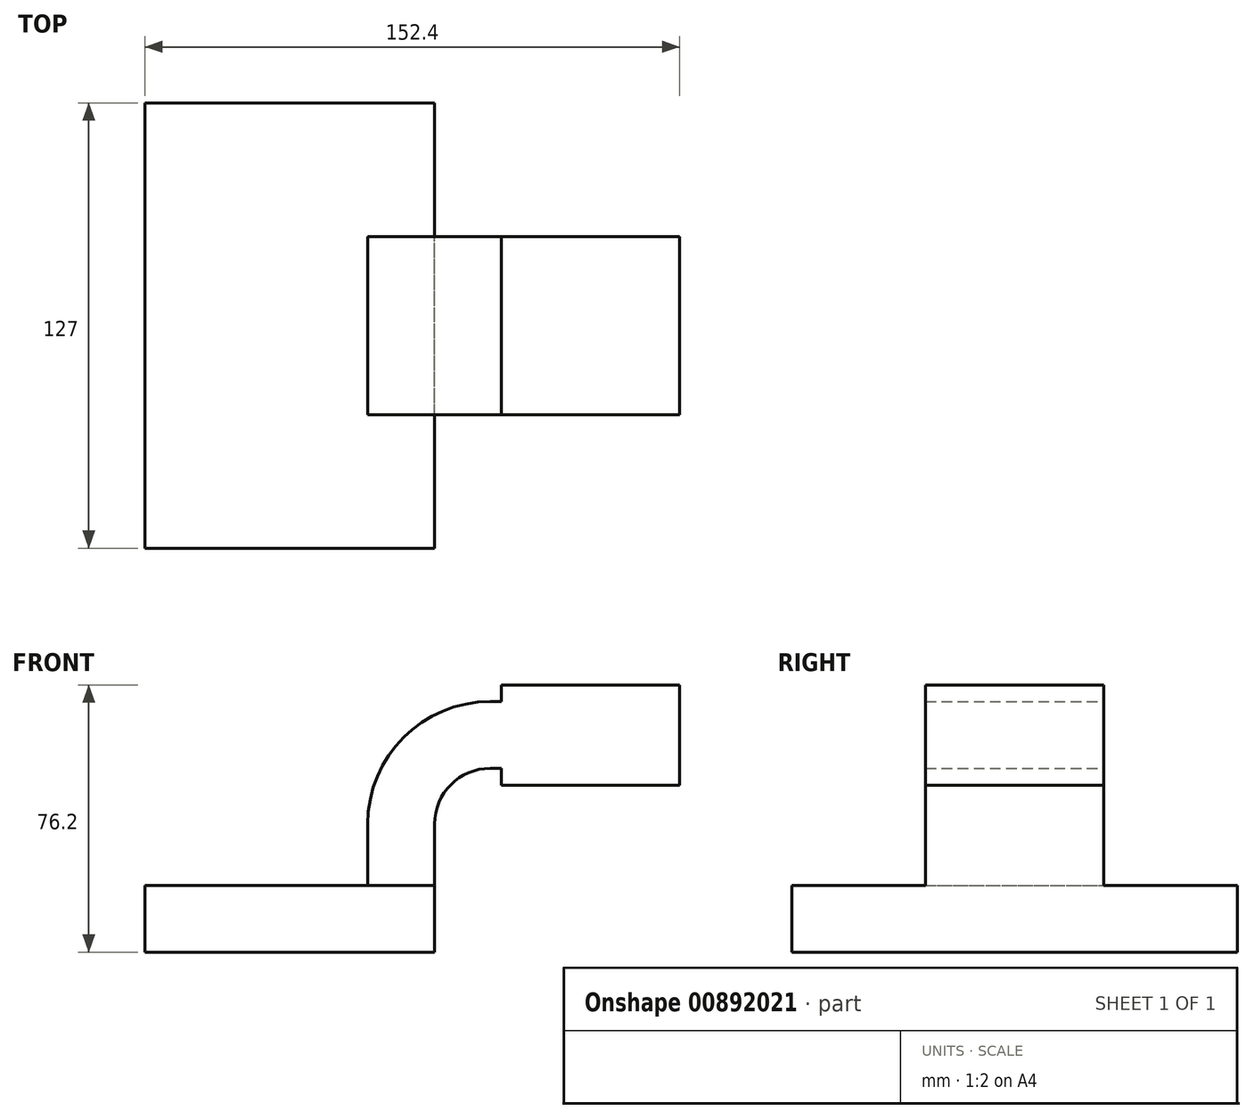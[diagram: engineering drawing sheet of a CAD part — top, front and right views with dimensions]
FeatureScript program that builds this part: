
annotation { "Feature Type Name" : "Feature", "Feature Type Description" : "" }
export const myFeature = defineFeature(function(context is Context, id is Id, definition is map)
    precondition{}
    {
        {
            var Q0;
            Q0=qCreatedBy(makeId("Front.planeOp"),FACE);
            var sketch = newSketch(context, id + "F0", { "sketchPlane" : qUnion([Q0])});
            skLineSegment(sketch, "E0.bottom", {"start": v(-41.28, 9.53) * mm, "end": v(41.28, 9.53) * mm});
            skLineSegment(sketch, "E0.top", {"start": v(-41.28, -9.52) * mm, "end": v(41.28, -9.52) * mm});
            skLineSegment(sketch, "E0.left", {"start": v(-41.28, 9.53) * mm, "end": v(-41.28, -9.52) * mm});
            skLineSegment(sketch, "E0.right", {"start": v(41.28, 9.53) * mm, "end": v(41.28, -9.52) * mm});
            skPoint(sketch, "E0.middle", {"position": v(0, 0) * mm});
            skLineSegment(sketch, "E1.bottom", {"start": v(60.33, 66.68) * mm, "end": v(111.12, 66.68) * mm});
            skLineSegment(sketch, "E1.top", {"start": v(60.33, 38.1) * mm, "end": v(111.12, 38.1) * mm});
            skLineSegment(sketch, "E1.left", {"start": v(60.33, 66.68) * mm, "end": v(60.33, 38.1) * mm});
            skLineSegment(sketch, "E1.right", {"start": v(111.12, 66.68) * mm, "end": v(111.12, 38.1) * mm});
            skPoint(sketch, "E1.middle", {"position": v(85.72, 52.39) * mm});
            skLineSegment(sketch, "E2", {"start": v(41.28, 9.53) * mm, "end": v(41.28, 27) * mm});
            skArc(sketch, "E3", {"start": v(41.28, 27) * mm, "mid": v(45.92, 38.23) * mm, "end": v(57.15, 42.88) * mm});
            skLineSegment(sketch, "E4", {"start": v(57.15, 42.88) * mm, "end": v(85.72, 42.88) * mm});
            skLineSegment(sketch, "E5.0", {"start": v(57.15, 61.93) * mm, "end": v(85.72, 61.93) * mm});
            skArc(sketch, "E5.1", {"start": v(22.23, 27) * mm, "mid": v(32.45, 51.7) * mm, "end": v(57.15, 61.93) * mm});
            skLineSegment(sketch, "E5.2", {"start": v(22.23, 9.53) * mm, "end": v(22.23, 27) * mm});
            skFitSpline(sketch, "E6", {"points": [v(-41.28, 9.53) * mm, v(57.15, 61.93) * mm], "startDerivative": vector(0, 54.02) * mm, "endDerivative": vector(171.45, 0) * mm});
            skLineSegment(sketch, "E7", {"start": v(85.72, 66.68) * mm, "end": v(85.72, 38.1) * mm});
            skSolve(sketch);
        }
        {
            var Q0;
            Q0=makeQuery(id+"F0.imprint","IMPRINT",FACE,{"disambiguationData":[TD([[makeQuery(id+"F0.imprint","IMPRINT",EDGE,{"derivedFrom":sQuery(id+"F0.wireOp",EDGE,"E0.top")}),1.0]])]});
            extrude(context, id + "F1", {"entities" : qUnion([Q0]), "endBound" : BoundingType.SYMMETRIC, "depth" : 127 * mm, "offsetDistance" : 25.4 * mm});
        }
        {
            var Q0;
            {var subQ1=sQuery(id+"F0.wireOp",EDGE,"E2");Q0=makeQuery(id+"F0.imprint","IMPRINT",FACE,{"disambiguationData":[TD([[makeQuery(id+"F0.imprint","IMPRINT",EDGE,{"derivedFrom":subQ1}),1.0]])]});}
            var Q1;
            {var subQ4=sQuery(id+"F0.wireOp",EDGE,"E1.right");Q1=makeQuery(id+"F0.imprint","IMPRINT",FACE,{"disambiguationData":[TD([[makeQuery(id+"F0.imprint","IMPRINT",EDGE,{"derivedFrom":subQ4}),-1.0]])]});}
            var Q2;
            {var subQ0=sQuery(id+"F0.wireOp",EDGE,"E5.0");var subQ1=sQuery(id+"F0.wireOp",EDGE,"E1.left");var subQ2=makeQuery(id+"F0.imprint","INTERSECT",VERTEX,{"derivedFrom":[subQ1,subQ0]});Q2=makeQuery(id+"F0.imprint","IMPRINT",FACE,{"disambiguationData":[TD([[makeQuery(id+"F0.imprint","IMPRINT",EDGE,{"disambiguationData":[TD([[subQ2,-1.0]])],"derivedFrom":subQ1}),1.0]])]});}
            var Q3;
            {var subQ0=sQuery(id+"F0.wireOp",EDGE,"E1.left");var subQ1=sQuery(id+"F0.wireOp",EDGE,"E1.bottom");var subQ2=makeQuery(id+"F0.imprint","INTERSECT",VERTEX,{"derivedFrom":[subQ1,subQ0]});Q3=makeQuery(id+"F0.imprint","IMPRINT",FACE,{"disambiguationData":[TD([[makeQuery(id+"F0.imprint","IMPRINT",EDGE,{"disambiguationData":[TD([[subQ2,-1.0]])],"derivedFrom":subQ1}),-1.0]])]});}
            var Q4;
            {var subQ0=sQuery(id+"F0.wireOp",EDGE,"E1.left");var subQ1=sQuery(id+"F0.wireOp",EDGE,"E1.top");var subQ2=makeQuery(id+"F0.imprint","INTERSECT",VERTEX,{"derivedFrom":[subQ1,subQ0]});Q4=makeQuery(id+"F0.imprint","IMPRINT",FACE,{"disambiguationData":[TD([[makeQuery(id+"F0.imprint","IMPRINT",EDGE,{"disambiguationData":[TD([[subQ2,-1.0]])],"derivedFrom":subQ1}),1.0]])]});}
            extrude(context, id + "F2", {"entities" : qUnion([Q0, Q1, Q2, Q3, Q4]), "operationType" : NewBodyOperationType.ADD, "endBound" : BoundingType.SYMMETRIC, "depth" : 50.8 * mm, "offsetDistance" : 25.4 * mm});
        }
    });
